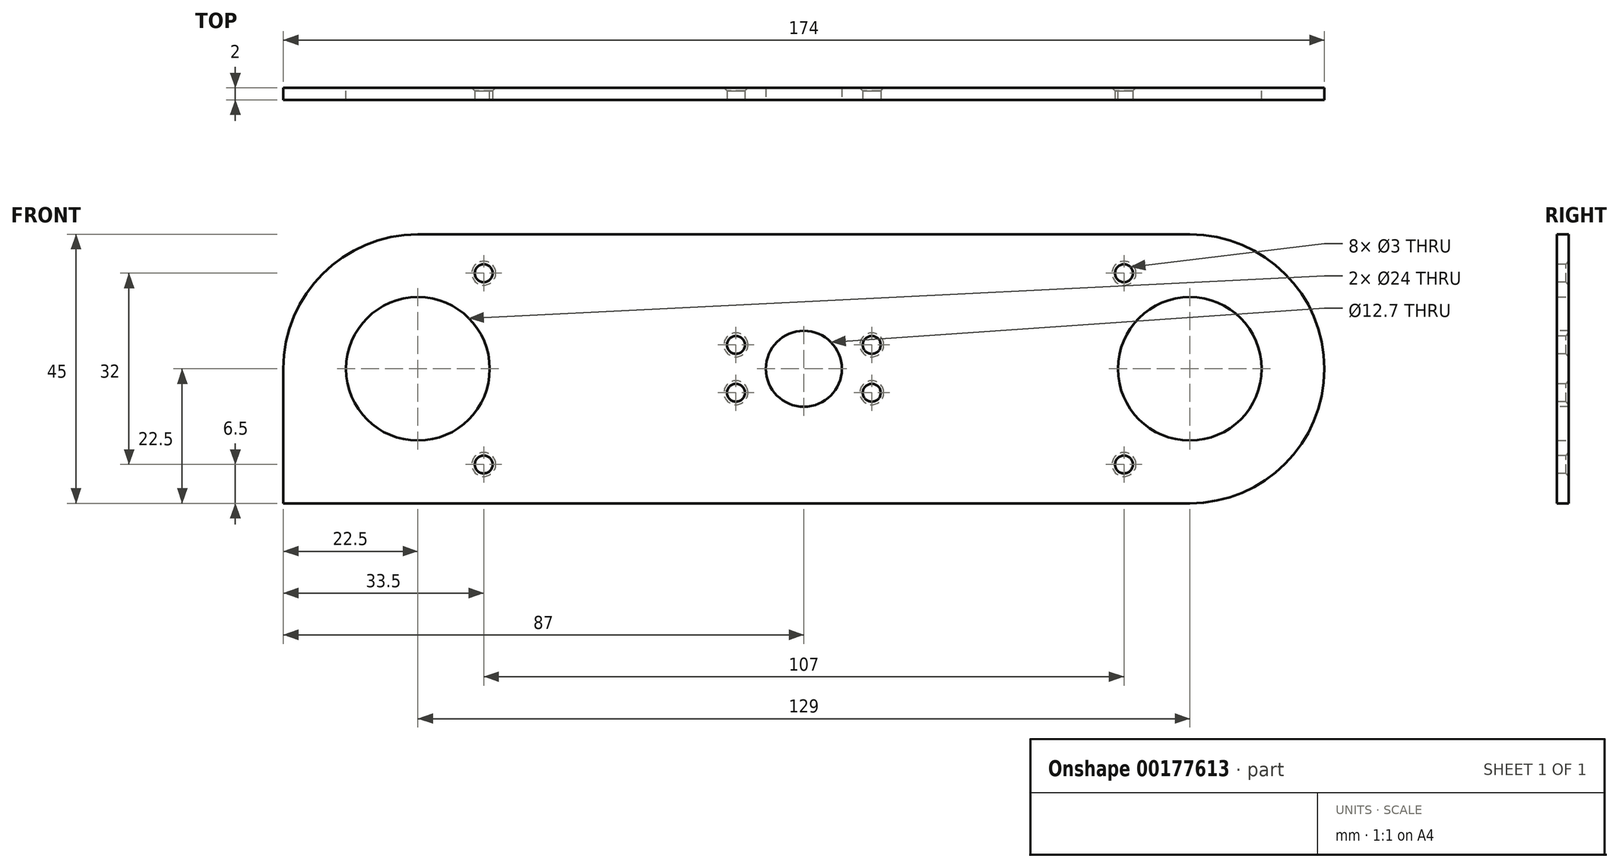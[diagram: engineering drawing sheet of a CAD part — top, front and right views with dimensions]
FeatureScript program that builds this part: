
annotation { "Feature Type Name" : "Feature", "Feature Type Description" : "" }
export const myFeature = defineFeature(function(context is Context, id is Id, definition is map)
    precondition{}
    {
        {
            var Q0;
            Q0=qCreatedBy(makeId("Front.planeOp"),FACE);
            var sketch = newSketch(context, id + "F0", { "sketchPlane" : qUnion([Q0])});
            skLineSegment(sketch, "E0.bottom", {"start": v(64.5, 22.5) * mm, "end": v(-64.5, 22.5) * mm});
            skLineSegment(sketch, "E0.top", {"start": v(64.5, -22.5) * mm, "end": v(-64.5, -22.5) * mm});
            skPoint(sketch, "E0.middle", {"position": v(0, 0) * mm});
            skCircle(sketch, "E1", {"center": v(64.5, 0) * mm, "radius": 12 * mm});
            skCircle(sketch, "E2", {"center": v(-64.5, 0) * mm, "radius": 12 * mm});
            skArc(sketch, "E3", {"start": v(-64.5, 22.5) * mm, "mid": v(-87, 0) * mm, "end": v(-64.5, -22.5) * mm});
            skArc(sketch, "E4", {"start": v(64.5, -22.5) * mm, "mid": v(87, 0) * mm, "end": v(64.5, 22.5) * mm});
            skPoint(sketch, "E5.orphan", {"position": v(-81.5, 22.5) * mm});
            skPoint(sketch, "E6.orphan", {"position": v(-81.5, -22.5) * mm});
            skPoint(sketch, "E7.orphan", {"position": v(81.5, 22.5) * mm});
            skPoint(sketch, "E8.orphan", {"position": v(81.5, -22.5) * mm});
            skSolve(sketch);
        }
        {
            var Q0;
            Q0=qSketchRegion(id+"F0",true);
            extrude(context, id + "F1", {"entities" : qUnion([Q0]), "depth" : 2 * mm});
        }
        {
            var Q0;
            Q0=makeQuery(id+"F1.opExtrude","CAP_FACE",FACE,{"disambiguationData":[OSD([sQuery(id+"F0.wireOp",EDGE,"E0.bottom"),sQuery(id+"F0.wireOp",EDGE,"E0.top"),sQuery(id+"F0.wireOp",EDGE,"E1"),sQuery(id+"F0.wireOp",EDGE,"E2"),sQuery(id+"F0.wireOp",EDGE,"E3"),sQuery(id+"F0.wireOp",EDGE,"E4")])],"isStart":false});
            var sketch = newSketch(context, id + "F2", { "sketchPlane" : qUnion([Q0])});
            skLineSegment(sketch, "E9.top", {"start": v(-64.5, -22.5) * mm, "end": v(-87, -22.5) * mm});
            skLineSegment(sketch, "E9.right", {"start": v(-87, 0) * mm, "end": v(-87, -22.5) * mm});
            skPoint(sketch, "E9.left.start.orphan", {"position": v(-64.5, 0) * mm});
            skLineSegment(sketch, "E10", {"start": v(-87, 0) * mm, "end": v(-80.88, 0) * mm});
            skLineSegment(sketch, "E11", {"start": v(-80.88, 0) * mm, "end": v(-78.27, -9.46) * mm});
            skLineSegment(sketch, "E12", {"start": v(-78.27, -9.46) * mm, "end": v(-70.55, -14.76) * mm});
            skLineSegment(sketch, "E13", {"start": v(-70.55, -14.76) * mm, "end": v(-64.5, -17.43) * mm});
            skLineSegment(sketch, "E14", {"start": v(-64.5, -17.43) * mm, "end": v(-64.5, -22.5) * mm});
            skSolve(sketch);
        }
        {
            var Q0;
            Q0=qSketchRegion(id+"F2",true);
            extrude(context, id + "F3", {"entities" : qUnion([Q0]), "operationType" : NewBodyOperationType.ADD, "oppositeDirection" : true, "depth" : 2 * mm});
        }
        {
            var Q0;
            Q0=makeQuery(id+"F3.boolean.opBoolean","MERGE",FACE,{"derivedFrom":[makeQuery(id+"F1.opExtrude","CAP_FACE",FACE,{"disambiguationData":[OSD([sQuery(id+"F0.wireOp",EDGE,"E0.bottom"),sQuery(id+"F0.wireOp",EDGE,"E0.top"),sQuery(id+"F0.wireOp",EDGE,"E1"),sQuery(id+"F0.wireOp",EDGE,"E2"),sQuery(id+"F0.wireOp",EDGE,"E3"),sQuery(id+"F0.wireOp",EDGE,"E4")])],"isStart":false}),makeQuery(id+"F3.opExtrude","CAP_FACE",FACE,{"disambiguationData":[OSD([sQuery(id+"F2.wireOp",EDGE,"E9.top"),sQuery(id+"F2.wireOp",EDGE,"E9.right"),sQuery(id+"F2.wireOp",EDGE,"E10"),sQuery(id+"F2.wireOp",EDGE,"E11"),sQuery(id+"F2.wireOp",EDGE,"E12"),sQuery(id+"F2.wireOp",EDGE,"E13"),sQuery(id+"F2.wireOp",EDGE,"E14")])],"isStart":true})]});
            var sketch = newSketch(context, id + "F4", { "sketchPlane" : qUnion([Q0])});
            skLineSegment(sketch, "E15.bottom", {"start": v(47, 22.5) * mm, "end": v(-47, 22.5) * mm, "construction": true});
            skLineSegment(sketch, "E15.top", {"start": v(47, -22.5) * mm, "end": v(-47, -22.5) * mm, "construction": true});
            skLineSegment(sketch, "E15.left", {"start": v(47, 22.5) * mm, "end": v(47, -22.5) * mm, "construction": true});
            skLineSegment(sketch, "E15.right", {"start": v(-47, 22.5) * mm, "end": v(-47, -22.5) * mm, "construction": true});
            skPoint(sketch, "E15.middle", {"position": v(0, 0) * mm});
            skLineSegment(sketch, "E16", {"start": v(-52.5, 0) * mm, "end": v(52.5, 0) * mm, "construction": true});
            skCircle(sketch, "E17", {"center": v(-53.5, 16) * mm, "radius": 1.5 * mm});
            skCircle(sketch, "E18", {"center": v(-53.5, -16) * mm, "radius": 1.5 * mm});
            skCircle(sketch, "E19", {"center": v(53.5, 16) * mm, "radius": 1.5 * mm});
            skCircle(sketch, "E20", {"center": v(53.5, -16) * mm, "radius": 1.5 * mm});
            skSolve(sketch);
        }
        {
            var Q0;
            Q0=qSketchRegion(id+"F4",true);
            extrude(context, id + "F5", {"entities" : qUnion([Q0]), "operationType" : NewBodyOperationType.REMOVE, "oppositeDirection" : true, "depth" : 25 * mm});
        }
        {
            var Q0;
            Q0=makeQuery(id+"F5.boolean.opBoolean","INTERSECT",EDGE,{"derivedFrom":[makeQuery(id+"F3.boolean.opBoolean","MERGE",FACE,{"derivedFrom":[makeQuery(id+"F1.opExtrude","CAP_FACE",FACE,{"disambiguationData":[OSD([sQuery(id+"F0.wireOp",EDGE,"E0.bottom"),sQuery(id+"F0.wireOp",EDGE,"E0.top"),sQuery(id+"F0.wireOp",EDGE,"E1"),sQuery(id+"F0.wireOp",EDGE,"E2"),sQuery(id+"F0.wireOp",EDGE,"E3"),sQuery(id+"F0.wireOp",EDGE,"E4")])],"isStart":true}),makeQuery(id+"F3.opExtrude","CAP_FACE",FACE,{"disambiguationData":[OSD([sQuery(id+"F2.wireOp",EDGE,"E9.top"),sQuery(id+"F2.wireOp",EDGE,"E9.right"),sQuery(id+"F2.wireOp",EDGE,"E10"),sQuery(id+"F2.wireOp",EDGE,"E11"),sQuery(id+"F2.wireOp",EDGE,"E12"),sQuery(id+"F2.wireOp",EDGE,"E13"),sQuery(id+"F2.wireOp",EDGE,"E14")])],"isStart":false})]}),makeQuery(id+"F5.opExtrude","SWEPT_FACE",FACE,{"disambiguationData":[OSD([sQuery(id+"F4.wireOp",EDGE,"E17")])]})]});
            var Q1;
            Q1=makeQuery(id+"F5.boolean.opBoolean","INTERSECT",EDGE,{"derivedFrom":[makeQuery(id+"F3.boolean.opBoolean","MERGE",FACE,{"derivedFrom":[makeQuery(id+"F1.opExtrude","CAP_FACE",FACE,{"disambiguationData":[OSD([sQuery(id+"F0.wireOp",EDGE,"E0.bottom"),sQuery(id+"F0.wireOp",EDGE,"E0.top"),sQuery(id+"F0.wireOp",EDGE,"E1"),sQuery(id+"F0.wireOp",EDGE,"E2"),sQuery(id+"F0.wireOp",EDGE,"E3"),sQuery(id+"F0.wireOp",EDGE,"E4")])],"isStart":true}),makeQuery(id+"F3.opExtrude","CAP_FACE",FACE,{"disambiguationData":[OSD([sQuery(id+"F2.wireOp",EDGE,"E9.top"),sQuery(id+"F2.wireOp",EDGE,"E9.right"),sQuery(id+"F2.wireOp",EDGE,"E10"),sQuery(id+"F2.wireOp",EDGE,"E11"),sQuery(id+"F2.wireOp",EDGE,"E12"),sQuery(id+"F2.wireOp",EDGE,"E13"),sQuery(id+"F2.wireOp",EDGE,"E14")])],"isStart":false})]}),makeQuery(id+"F5.opExtrude","SWEPT_FACE",FACE,{"disambiguationData":[OSD([sQuery(id+"F4.wireOp",EDGE,"E18")])]})]});
            var Q2;
            Q2=makeQuery(id+"F5.boolean.opBoolean","INTERSECT",EDGE,{"derivedFrom":[makeQuery(id+"F3.boolean.opBoolean","MERGE",FACE,{"derivedFrom":[makeQuery(id+"F1.opExtrude","CAP_FACE",FACE,{"disambiguationData":[OSD([sQuery(id+"F0.wireOp",EDGE,"E0.bottom"),sQuery(id+"F0.wireOp",EDGE,"E0.top"),sQuery(id+"F0.wireOp",EDGE,"E1"),sQuery(id+"F0.wireOp",EDGE,"E2"),sQuery(id+"F0.wireOp",EDGE,"E3"),sQuery(id+"F0.wireOp",EDGE,"E4")])],"isStart":true}),makeQuery(id+"F3.opExtrude","CAP_FACE",FACE,{"disambiguationData":[OSD([sQuery(id+"F2.wireOp",EDGE,"E9.top"),sQuery(id+"F2.wireOp",EDGE,"E9.right"),sQuery(id+"F2.wireOp",EDGE,"E10"),sQuery(id+"F2.wireOp",EDGE,"E11"),sQuery(id+"F2.wireOp",EDGE,"E12"),sQuery(id+"F2.wireOp",EDGE,"E13"),sQuery(id+"F2.wireOp",EDGE,"E14")])],"isStart":false})]}),makeQuery(id+"F5.opExtrude","SWEPT_FACE",FACE,{"disambiguationData":[OSD([sQuery(id+"F4.wireOp",EDGE,"E19")])]})]});
            var Q3;
            Q3=makeQuery(id+"F5.boolean.opBoolean","INTERSECT",EDGE,{"derivedFrom":[makeQuery(id+"F3.boolean.opBoolean","MERGE",FACE,{"derivedFrom":[makeQuery(id+"F1.opExtrude","CAP_FACE",FACE,{"disambiguationData":[OSD([sQuery(id+"F0.wireOp",EDGE,"E0.bottom"),sQuery(id+"F0.wireOp",EDGE,"E0.top"),sQuery(id+"F0.wireOp",EDGE,"E1"),sQuery(id+"F0.wireOp",EDGE,"E2"),sQuery(id+"F0.wireOp",EDGE,"E3"),sQuery(id+"F0.wireOp",EDGE,"E4")])],"isStart":true}),makeQuery(id+"F3.opExtrude","CAP_FACE",FACE,{"disambiguationData":[OSD([sQuery(id+"F2.wireOp",EDGE,"E9.top"),sQuery(id+"F2.wireOp",EDGE,"E9.right"),sQuery(id+"F2.wireOp",EDGE,"E10"),sQuery(id+"F2.wireOp",EDGE,"E11"),sQuery(id+"F2.wireOp",EDGE,"E12"),sQuery(id+"F2.wireOp",EDGE,"E13"),sQuery(id+"F2.wireOp",EDGE,"E14")])],"isStart":false})]}),makeQuery(id+"F5.opExtrude","SWEPT_FACE",FACE,{"disambiguationData":[OSD([sQuery(id+"F4.wireOp",EDGE,"E20")])]})]});
            chamfer(context, id + "F6", {"entities" : qUnion([Q0, Q1, Q2, Q3]), "width" : .5 * mm, "tangentPropagation" : true});
        }
        {
            var Q0;
            Q0=makeQuery(id+"F3.boolean.opBoolean","MERGE",FACE,{"derivedFrom":[makeQuery(id+"F1.opExtrude","CAP_FACE",FACE,{"disambiguationData":[OSD([sQuery(id+"F0.wireOp",EDGE,"E0.bottom"),sQuery(id+"F0.wireOp",EDGE,"E0.top"),sQuery(id+"F0.wireOp",EDGE,"E1"),sQuery(id+"F0.wireOp",EDGE,"E2"),sQuery(id+"F0.wireOp",EDGE,"E3"),sQuery(id+"F0.wireOp",EDGE,"E4")])],"isStart":false}),makeQuery(id+"F3.opExtrude","CAP_FACE",FACE,{"disambiguationData":[OSD([sQuery(id+"F2.wireOp",EDGE,"E9.top"),sQuery(id+"F2.wireOp",EDGE,"E9.right"),sQuery(id+"F2.wireOp",EDGE,"E10"),sQuery(id+"F2.wireOp",EDGE,"E11"),sQuery(id+"F2.wireOp",EDGE,"E12"),sQuery(id+"F2.wireOp",EDGE,"E13"),sQuery(id+"F2.wireOp",EDGE,"E14")])],"isStart":true})]});
            var sketch = newSketch(context, id + "F7", { "sketchPlane" : qUnion([Q0])});
            skCircle(sketch, "E21", {"center": v(0, 0) * mm, "radius": 6.35 * mm});
            skSolve(sketch);
        }
        {
            var Q0;
            Q0=qSketchRegion(id+"F7",true);
            extrude(context, id + "F8", {"entities" : qUnion([Q0]), "operationType" : NewBodyOperationType.REMOVE, "oppositeDirection" : true, "depth" : 25 * mm});
        }
        {
            var Q0;
            Q0=makeQuery(id+"F3.boolean.opBoolean","MERGE",FACE,{"derivedFrom":[makeQuery(id+"F1.opExtrude","CAP_FACE",FACE,{"disambiguationData":[OSD([sQuery(id+"F0.wireOp",EDGE,"E0.bottom"),sQuery(id+"F0.wireOp",EDGE,"E0.top"),sQuery(id+"F0.wireOp",EDGE,"E1"),sQuery(id+"F0.wireOp",EDGE,"E2"),sQuery(id+"F0.wireOp",EDGE,"E3"),sQuery(id+"F0.wireOp",EDGE,"E4")])],"isStart":false}),makeQuery(id+"F3.opExtrude","CAP_FACE",FACE,{"disambiguationData":[OSD([sQuery(id+"F2.wireOp",EDGE,"E9.top"),sQuery(id+"F2.wireOp",EDGE,"E9.right"),sQuery(id+"F2.wireOp",EDGE,"E10"),sQuery(id+"F2.wireOp",EDGE,"E11"),sQuery(id+"F2.wireOp",EDGE,"E12"),sQuery(id+"F2.wireOp",EDGE,"E13"),sQuery(id+"F2.wireOp",EDGE,"E14")])],"isStart":true})]});
            var sketch = newSketch(context, id + "F9", { "sketchPlane" : qUnion([Q0])});
            skPoint(sketch, "E22.middle", {"position": v(0, 0) * mm});
            skCircle(sketch, "E23", {"center": v(-11.35, 4) * mm, "radius": 1.5 * mm});
            skCircle(sketch, "E24", {"center": v(-11.35, -4) * mm, "radius": 1.5 * mm});
            skCircle(sketch, "E25", {"center": v(11.35, 4) * mm, "radius": 1.5 * mm});
            skCircle(sketch, "E26", {"center": v(11.35, -4) * mm, "radius": 1.5 * mm});
            skPoint(sketch, "E27.orphan", {"position": v(-11.35, 11.35) * mm});
            skPoint(sketch, "E28.orphan", {"position": v(11.35, 11.35) * mm});
            skPoint(sketch, "E22.top.start.orphan", {"position": v(11.35, -11.35) * mm});
            skPoint(sketch, "E29.orphan", {"position": v(-11.35, -11.35) * mm});
            skLineSegment(sketch, "E30", {"start": v(52.5, 0) * mm, "end": v(-52.5, 0) * mm, "construction": true});
            skLineSegment(sketch, "E31", {"start": v(-52.5, 0) * mm, "end": v(0, 0) * mm, "construction": true});
            skLineSegment(sketch, "E32", {"start": v(0, 22.5) * mm, "end": v(0, -22.5) * mm, "construction": true});
            skLineSegment(sketch, "E33.bottom", {"start": v(11.35, 11.35) * mm, "end": v(-11.35, 11.35) * mm, "construction": true});
            skLineSegment(sketch, "E33.top", {"start": v(11.35, -11.35) * mm, "end": v(-11.35, -11.35) * mm, "construction": true});
            skLineSegment(sketch, "E33.left", {"start": v(11.35, 11.35) * mm, "end": v(11.35, -11.35) * mm, "construction": true});
            skLineSegment(sketch, "E33.right", {"start": v(-11.35, 11.35) * mm, "end": v(-11.35, -11.35) * mm, "construction": true});
            skSolve(sketch);
        }
        {
            var Q0;
            Q0=qSketchRegion(id+"F9",true);
            extrude(context, id + "F10", {"entities" : qUnion([Q0]), "operationType" : NewBodyOperationType.REMOVE, "oppositeDirection" : true, "depth" : 25 * mm});
        }
        {
            var Q0;
            Q0=makeQuery(id+"F10.boolean.opBoolean","INTERSECT",EDGE,{"derivedFrom":[makeQuery(id+"F3.boolean.opBoolean","MERGE",FACE,{"derivedFrom":[makeQuery(id+"F1.opExtrude","CAP_FACE",FACE,{"disambiguationData":[OSD([sQuery(id+"F0.wireOp",EDGE,"E0.bottom"),sQuery(id+"F0.wireOp",EDGE,"E0.top"),sQuery(id+"F0.wireOp",EDGE,"E1"),sQuery(id+"F0.wireOp",EDGE,"E2"),sQuery(id+"F0.wireOp",EDGE,"E3"),sQuery(id+"F0.wireOp",EDGE,"E4")])],"isStart":true}),makeQuery(id+"F3.opExtrude","CAP_FACE",FACE,{"disambiguationData":[OSD([sQuery(id+"F2.wireOp",EDGE,"E9.top"),sQuery(id+"F2.wireOp",EDGE,"E9.right"),sQuery(id+"F2.wireOp",EDGE,"E10"),sQuery(id+"F2.wireOp",EDGE,"E11"),sQuery(id+"F2.wireOp",EDGE,"E12"),sQuery(id+"F2.wireOp",EDGE,"E13"),sQuery(id+"F2.wireOp",EDGE,"E14")])],"isStart":false})]}),makeQuery(id+"F10.opExtrude","SWEPT_FACE",FACE,{"disambiguationData":[OSD([sQuery(id+"F9.wireOp",EDGE,"E23")])]})]});
            var Q1;
            Q1=makeQuery(id+"F10.boolean.opBoolean","INTERSECT",EDGE,{"derivedFrom":[makeQuery(id+"F3.boolean.opBoolean","MERGE",FACE,{"derivedFrom":[makeQuery(id+"F1.opExtrude","CAP_FACE",FACE,{"disambiguationData":[OSD([sQuery(id+"F0.wireOp",EDGE,"E0.bottom"),sQuery(id+"F0.wireOp",EDGE,"E0.top"),sQuery(id+"F0.wireOp",EDGE,"E1"),sQuery(id+"F0.wireOp",EDGE,"E2"),sQuery(id+"F0.wireOp",EDGE,"E3"),sQuery(id+"F0.wireOp",EDGE,"E4")])],"isStart":true}),makeQuery(id+"F3.opExtrude","CAP_FACE",FACE,{"disambiguationData":[OSD([sQuery(id+"F2.wireOp",EDGE,"E9.top"),sQuery(id+"F2.wireOp",EDGE,"E9.right"),sQuery(id+"F2.wireOp",EDGE,"E10"),sQuery(id+"F2.wireOp",EDGE,"E11"),sQuery(id+"F2.wireOp",EDGE,"E12"),sQuery(id+"F2.wireOp",EDGE,"E13"),sQuery(id+"F2.wireOp",EDGE,"E14")])],"isStart":false})]}),makeQuery(id+"F10.opExtrude","SWEPT_FACE",FACE,{"disambiguationData":[OSD([sQuery(id+"F9.wireOp",EDGE,"E24")])]})]});
            var Q2;
            Q2=makeQuery(id+"F10.boolean.opBoolean","INTERSECT",EDGE,{"derivedFrom":[makeQuery(id+"F3.boolean.opBoolean","MERGE",FACE,{"derivedFrom":[makeQuery(id+"F1.opExtrude","CAP_FACE",FACE,{"disambiguationData":[OSD([sQuery(id+"F0.wireOp",EDGE,"E0.bottom"),sQuery(id+"F0.wireOp",EDGE,"E0.top"),sQuery(id+"F0.wireOp",EDGE,"E1"),sQuery(id+"F0.wireOp",EDGE,"E2"),sQuery(id+"F0.wireOp",EDGE,"E3"),sQuery(id+"F0.wireOp",EDGE,"E4")])],"isStart":true}),makeQuery(id+"F3.opExtrude","CAP_FACE",FACE,{"disambiguationData":[OSD([sQuery(id+"F2.wireOp",EDGE,"E9.top"),sQuery(id+"F2.wireOp",EDGE,"E9.right"),sQuery(id+"F2.wireOp",EDGE,"E10"),sQuery(id+"F2.wireOp",EDGE,"E11"),sQuery(id+"F2.wireOp",EDGE,"E12"),sQuery(id+"F2.wireOp",EDGE,"E13"),sQuery(id+"F2.wireOp",EDGE,"E14")])],"isStart":false})]}),makeQuery(id+"F10.opExtrude","SWEPT_FACE",FACE,{"disambiguationData":[OSD([sQuery(id+"F9.wireOp",EDGE,"E26")])]})]});
            var Q3;
            Q3=makeQuery(id+"F10.boolean.opBoolean","INTERSECT",EDGE,{"derivedFrom":[makeQuery(id+"F3.boolean.opBoolean","MERGE",FACE,{"derivedFrom":[makeQuery(id+"F1.opExtrude","CAP_FACE",FACE,{"disambiguationData":[OSD([sQuery(id+"F0.wireOp",EDGE,"E0.bottom"),sQuery(id+"F0.wireOp",EDGE,"E0.top"),sQuery(id+"F0.wireOp",EDGE,"E1"),sQuery(id+"F0.wireOp",EDGE,"E2"),sQuery(id+"F0.wireOp",EDGE,"E3"),sQuery(id+"F0.wireOp",EDGE,"E4")])],"isStart":true}),makeQuery(id+"F3.opExtrude","CAP_FACE",FACE,{"disambiguationData":[OSD([sQuery(id+"F2.wireOp",EDGE,"E9.top"),sQuery(id+"F2.wireOp",EDGE,"E9.right"),sQuery(id+"F2.wireOp",EDGE,"E10"),sQuery(id+"F2.wireOp",EDGE,"E11"),sQuery(id+"F2.wireOp",EDGE,"E12"),sQuery(id+"F2.wireOp",EDGE,"E13"),sQuery(id+"F2.wireOp",EDGE,"E14")])],"isStart":false})]}),makeQuery(id+"F10.opExtrude","SWEPT_FACE",FACE,{"disambiguationData":[OSD([sQuery(id+"F9.wireOp",EDGE,"E25")])]})]});
            chamfer(context, id + "F11", {"entities" : qUnion([Q0, Q1, Q2, Q3]), "width" : .5 * mm, "tangentPropagation" : true});
        }
    });
